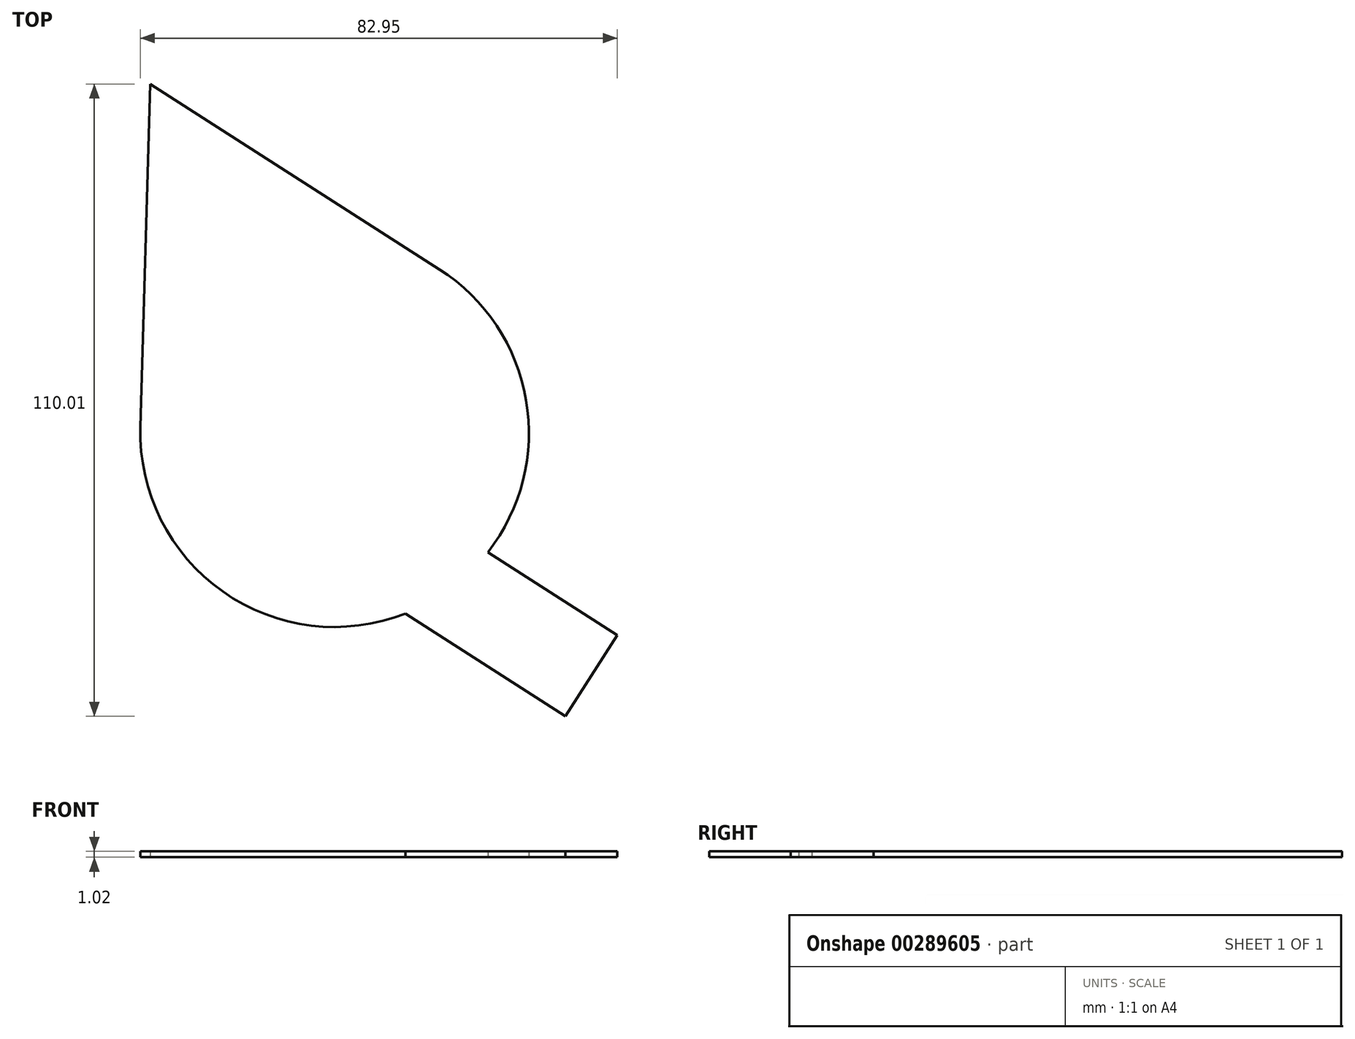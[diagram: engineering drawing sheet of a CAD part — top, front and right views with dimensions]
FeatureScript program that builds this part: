
annotation { "Feature Type Name" : "Feature", "Feature Type Description" : "" }
export const myFeature = defineFeature(function(context is Context, id is Id, definition is map)
    precondition{}
    {
        {
            var Q0;
            Q0=qCreatedBy(makeId("Top.planeOp"),FACE);
            var sketch = newSketch(context, id + "F0", { "sketchPlane" : qUnion([Q0])});
            skLineSegment(sketch, "E0.0", {"start": v(-54.42, 51.92) * mm, "end": v(-4.14, 19.66) * mm});
            skArc(sketch, "E0.1", {"start": v(11.4, -8.77) * mm, "mid": v(7.26, 7.43) * mm, "end": v(-4.14, 19.66) * mm});
            skLineSegment(sketch, "E0.2", {"start": v(-54.42, 51.92) * mm, "end": v(-56.15, -7.8) * mm});
            skArc(sketch, "E0.3", {"start": v(4.27, -29.53) * mm, "mid": v(9.57, -19.75) * mm, "end": v(11.4, -8.77) * mm});
            skArc(sketch, "E0.4", {"start": v(-56.15, -7.8) * mm, "mid": v(-41.84, -36.39) * mm, "end": v(-10.1, -40.24) * mm});
            skLineSegment(sketch, "E0.5", {"start": v(-10.1, -40.24) * mm, "end": v(17.74, -58.1) * mm});
            skLineSegment(sketch, "E0.6", {"start": v(26.8, -43.98) * mm, "end": v(17.74, -58.1) * mm});
            skLineSegment(sketch, "E0.7", {"start": v(26.8, -43.98) * mm, "end": v(4.27, -29.53) * mm});
            skSolve(sketch);
        }
        {
            var Q0;
            Q0=makeQuery(id+"F0.imprint","IMPRINT",FACE,{"disambiguationData":[TD([[makeQuery(id+"F0.imprint","IMPRINT",EDGE,{"derivedFrom":sQuery(id+"F0.wireOp",EDGE,"E0.0")}),-1.0]])]});
            extrude(context, id + "F1", {"entities" : qUnion([Q0]), "depth" : 1.02 * mm});
        }
    });
